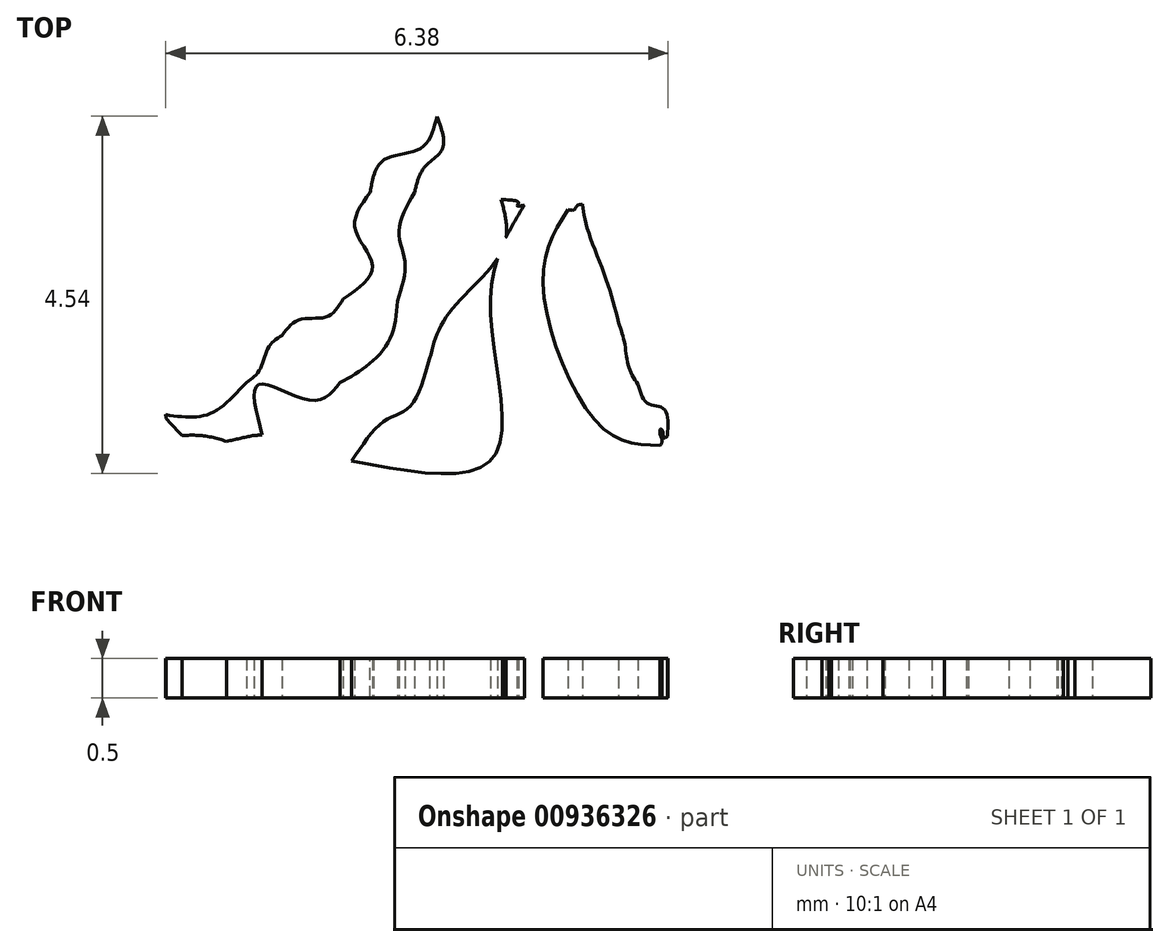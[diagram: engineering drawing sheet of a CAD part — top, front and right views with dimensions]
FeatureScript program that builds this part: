
annotation { "Feature Type Name" : "Feature", "Feature Type Description" : "" }
export const myFeature = defineFeature(function(context is Context, id is Id, definition is map)
    precondition{}
    {
        {
            var Q0;
            Q0=qCreatedBy(makeId("Top.planeOp"),FACE);
            var sketch = newSketch(context, id + "F0", { "sketchPlane" : qUnion([Q0])});
            skFitSpline(sketch, "E0", {"points": [v(-1.48, -0.63) * mm, v(-1.68, -1.04) * mm, v(-2.15, -1.19) * mm, v(-2.32, -1.6) * mm]});
            skFitSpline(sketch, "E1", {"points": [v(-2.32, -1.6) * mm, v(-2.51, -2.06) * mm, v(-2.3, -2.54) * mm, v(-2.66, -2.95) * mm]});
            skFitSpline(sketch, "E2", {"points": [v(-2.66, -2.95) * mm, v(-2.87, -3.18) * mm, v(-3.21, -3.21) * mm, v(-3.44, -3.41) * mm]});
            skFitSpline(sketch, "E3", {"points": [v(-3.44, -3.41) * mm, v(-3.61, -3.57) * mm, v(-3.73, -3.86) * mm, v(-3.9, -4.01) * mm]});
            skFitSpline(sketch, "E4", {"points": [v(-3.9, -4.01) * mm, v(-4.26, -4.36) * mm, v(-4.55, -4.45) * mm, v(-4.92, -4.42) * mm]});
            skFitSpline(sketch, "E5", {"points": [v(-4.92, -4.42) * mm, v(-4.92, -4.44) * mm, v(-4.92, -4.46) * mm, v(-4.91, -4.47) * mm]});
            skFitSpline(sketch, "E6", {"points": [v(-4.91, -4.47) * mm, v(-4.85, -4.55) * mm, v(-4.78, -4.62) * mm, v(-4.71, -4.69) * mm]});
            skFitSpline(sketch, "E7", {"points": [v(-4.71, -4.69) * mm, v(-4.52, -4.69) * mm, v(-4.33, -4.71) * mm, v(-4.15, -4.76) * mm]});
            skFitSpline(sketch, "E8", {"points": [v(-4.15, -4.76) * mm, v(-3.97, -4.72) * mm, v(-3.81, -4.69) * mm, v(-3.7, -4.68) * mm]});
            skFitSpline(sketch, "E9", {"points": [v(-3.7, -4.68) * mm, v(-3.74, -4.04) * mm, v(-3.06, -4.24) * mm, v(-2.7, -4.02) * mm]});
            skFitSpline(sketch, "E10", {"points": [v(-2.7, -4.02) * mm, v(-2.36, -3.8) * mm, v(-2.07, -3.45) * mm, v(-1.98, -2.98) * mm]});
            skFitSpline(sketch, "E11", {"points": [v(-1.98, -2.98) * mm, v(-1.88, -2.48) * mm, v(-1.96, -2.1) * mm, v(-1.76, -1.6) * mm]});
            skFitSpline(sketch, "E12", {"points": [v(-1.76, -1.6) * mm, v(-1.63, -1.28) * mm, v(-1.4, -1.04) * mm, v(-1.48, -0.63) * mm]});
            skFitSpline(sketch, "E13", {"points": [v(3.94, -4.49) * mm, v(3.82, -4.17) * mm, v(3.68, -3.64) * mm, v(3.43, -3.44) * mm]});
            skFitSpline(sketch, "E14", {"points": [v(3.43, -3.44) * mm, v(3.22, -3.27) * mm, v(2.85, -3.43) * mm, v(2.63, -3.2) * mm]});
            skFitSpline(sketch, "E15", {"points": [v(2.63, -3.2) * mm, v(2.34, -2.93) * mm, v(2.34, -2.3) * mm, v(2.2, -1.94) * mm]});
            skFitSpline(sketch, "E16", {"points": [v(2.2, -1.94) * mm, v(1.93, -1.29) * mm, v(1.3, -1.13) * mm, v(1.27, -0.36) * mm]});
            skFitSpline(sketch, "E17", {"points": [v(0.7, -0.56) * mm, v(1.13, -0.9) * mm, v(1.23, -1.34) * mm, v(1.43, -1.84) * mm]});
            skFitSpline(sketch, "E18", {"points": [v(1.43, -1.84) * mm, v(1.58, -2.21) * mm, v(1.64, -2.69) * mm, v(1.8, -3.03) * mm]});
            skFitSpline(sketch, "E19", {"points": [v(1.8, -3.03) * mm, v(2.08, -3.57) * mm, v(2.64, -3.47) * mm, v(3, -3.87) * mm]});
            skFitSpline(sketch, "E20", {"points": [v(3, -3.87) * mm, v(3.29, -4.18) * mm, v(3.34, -4.74) * mm, v(3.94, -4.49) * mm]});
            skFitSpline(sketch, "E21", {"points": [v(-2.15, -1.57) * mm, v(-2.53, -1) * mm, v(-2.79, -0.73) * mm, v(-3.39, -0.68) * mm]});
            skFitSpline(sketch, "E22", {"points": [v(-3.39, -0.68) * mm, v(-3.76, -0.65) * mm, v(-3.98, -0.73) * mm, v(-4.31, -0.48) * mm]});
            skFitSpline(sketch, "E23", {"points": [v(-4.31, -0.48) * mm, v(-4.88, -0.04) * mm, v(-5.85, 0.8) * mm, v(-4.97, 1.37) * mm]});
            skFitSpline(sketch, "E24", {"points": [v(-4.97, 1.37) * mm, v(-4.12, 1.92) * mm, v(-3.04, 1.34) * mm, v(-2.15, 1.29) * mm]});
            skFitSpline(sketch, "E25", {"points": [v(-2.15, 1.29) * mm, v(-1.68, 1.26) * mm, v(-1.22, 1.44) * mm, v(-0.78, 1.43) * mm]});
            skFitSpline(sketch, "E26", {"points": [v(-0.78, 1.43) * mm, v(-0.29, 1.41) * mm, v(0.03, 1.23) * mm, v(0.53, 1.3) * mm]});
            skFitSpline(sketch, "E27", {"points": [v(0.53, 1.3) * mm, v(1.17, 1.37) * mm, v(1.83, 1.4) * mm, v(2.46, 1.22) * mm]});
            skFitSpline(sketch, "E28", {"points": [v(2.46, 1.22) * mm, v(3.17, 1) * mm, v(3.92, 1.01) * mm, v(4.67, 0.94) * mm]});
            skFitSpline(sketch, "E29", {"points": [v(4.67, 0.94) * mm, v(4.73, -0.3) * mm, v(0.98, 0.89) * mm, v(0.38, 0.95) * mm]});
            skFitSpline(sketch, "E30", {"points": [v(-2.46, 0.88) * mm, v(-3.42, 0.83) * mm, v(-4.37, 1.02) * mm, v(-5.33, 1.02) * mm]});
            skFitSpline(sketch, "E31", {"points": [v(0.98, -0.68) * mm, v(1.32, -0.55) * mm, v(1.54, -0.76) * mm, v(1.84, -0.74) * mm]});
            skFitSpline(sketch, "E32", {"points": [v(1.84, -0.74) * mm, v(2.25, -0.71) * mm, v(2.7, -0.42) * mm, v(3.09, -0.27) * mm]});
            skFitSpline(sketch, "E33", {"points": [v(3.09, -0.27) * mm, v(3.47, -0.12) * mm, v(4.31, 0.08) * mm, v(4.44, 0.6) * mm]});
            skFitSpline(sketch, "E34", {"points": [v(2.47, 0.16) * mm, v(2, 0) * mm, v(1.5, -0.5) * mm, v(0.98, -0.68) * mm]});
            skFitSpline(sketch, "E35", {"points": [v(-1.92, -1.23) * mm, v(-1.14, -1.23) * mm, v(-0.57, -1.05) * mm, v(0.17, -0.95) * mm]});
            skFitSpline(sketch, "E36", {"points": [v(0.17, -0.95) * mm, v(0.44, -0.92) * mm, v(1.05, -1.18) * mm, v(1.27, -1.01) * mm]});
            skFitSpline(sketch, "E37", {"points": [v(1.27, -1.01) * mm, v(1.76, -0.64) * mm, v(0.1, -0.55) * mm, v(-0.01, -0.55) * mm]});
            skFitSpline(sketch, "E38", {"points": [v(-3.42, 3.67) * mm, v(-3.16, 3.86) * mm, v(-3.05, 4.17) * mm, v(-2.82, 4.4) * mm]});
            skFitSpline(sketch, "E39", {"points": [v(-2.82, 4.4) * mm, v(-2.53, 4.7) * mm, v(-2.27, 4.78) * mm, v(-1.86, 4.92) * mm]});
            skFitSpline(sketch, "E40", {"points": [v(-1.86, 4.92) * mm, v(-1.22, 5.15) * mm, v(-0.68, 5.33) * mm, v(0.04, 5.24) * mm]});
            skFitSpline(sketch, "E41", {"points": [v(0.04, 5.24) * mm, v(0.42, 5.2) * mm, v(0.38, 5.22) * mm, v(0.65, 5.07) * mm]});
            skFitSpline(sketch, "E42", {"points": [v(0.65, 5.07) * mm, v(0.9, 4.93) * mm, v(0.97, 4.7) * mm, v(1.27, 4.63) * mm]});
            skFitSpline(sketch, "E43", {"points": [v(1.27, 4.63) * mm, v(1.68, 4.54) * mm, v(1.95, 4.72) * mm, v(2.32, 4.41) * mm]});
            skFitSpline(sketch, "E44", {"points": [v(2.32, 4.41) * mm, v(2.64, 4.15) * mm, v(3.12, 3.3) * mm, v(3.07, 2.9) * mm]});
            skFitSpline(sketch, "E45", {"points": [v(3.07, 2.9) * mm, v(2.9, 3.08) * mm, v(2.63, 3.17) * mm, v(2.37, 3.14) * mm]});
            skFitSpline(sketch, "E46", {"points": [v(2.37, 3.14) * mm, v(2.35, 3.7) * mm, v(1.28, 4.03) * mm, v(0.85, 4.22) * mm]});
            skFitSpline(sketch, "E47", {"points": [v(0.85, 4.22) * mm, v(0.22, 4.5) * mm, v(-0.55, 4.69) * mm, v(-1.26, 4.55) * mm]});
            skFitSpline(sketch, "E48", {"points": [v(-1.26, 4.55) * mm, v(-1.86, 4.43) * mm, v(-2.25, 4.18) * mm, v(-2.68, 3.8) * mm]});
            skFitSpline(sketch, "E49", {"points": [v(-2.68, 3.8) * mm, v(-2.96, 3.55) * mm, v(-3.39, 2.9) * mm, v(-3.78, 2.9) * mm]});
            skFitSpline(sketch, "E50", {"points": [v(-3.78, 2.9) * mm, v(-3.93, 3.44) * mm, v(-3.3, 3.45) * mm, v(-3.42, 3.67) * mm]});
            skFitSpline(sketch, "E51", {"points": [v(-0.66, -1.69) * mm, v(-0.64, -2.32) * mm, v(-1.32, -3.14) * mm, v(-1.57, -3.7) * mm]});
            skFitSpline(sketch, "E52", {"points": [v(-1.57, -3.7) * mm, v(-1.83, -4.34) * mm, v(-2.13, -4.5) * mm, v(-2.56, -5.01) * mm]});
            skFitSpline(sketch, "E53", {"points": [v(-2.56, -5.01) * mm, v(-0.75, -4.95) * mm, v(-0.8, -3.01) * mm, v(-0.36, -1.76) * mm]});
            skFitSpline(sketch, "E54", {"points": [v(-0.36, -1.76) * mm, v(-0.45, -1.77) * mm, v(-0.44, -1.73) * mm, v(-0.66, -1.69) * mm]});
            skFitSpline(sketch, "E55", {"points": [v(0.37, -1.75) * mm, v(0.3, -1.77) * mm, v(0.27, -1.82) * mm, v(0.2, -1.82) * mm]});
            skFitSpline(sketch, "E56", {"points": [v(0.2, -1.82) * mm, v(-0.13, -2.74) * mm, v(0.63, -4.59) * mm, v(1.36, -4.81) * mm]});
            skFitSpline(sketch, "E57", {"points": [v(1.36, -4.81) * mm, v(1.39, -4.76) * mm, v(1.36, -4.66) * mm, v(1.36, -4.6) * mm]});
            skFitSpline(sketch, "E58", {"points": [v(1.36, -4.6) * mm, v(1.39, -4.62) * mm, v(1.4, -4.72) * mm, v(1.45, -4.7) * mm]});
            skFitSpline(sketch, "E59", {"points": [v(1.45, -4.7) * mm, v(1.4, -4.35) * mm, v(1.2, -4.28) * mm, v(1.08, -4.04) * mm]});
            skFitSpline(sketch, "E60", {"points": [v(1.08, -4.04) * mm, v(0.96, -3.8) * mm, v(0.91, -3.52) * mm, v(0.83, -3.26) * mm]});
            skFitSpline(sketch, "E61", {"points": [v(0.83, -3.26) * mm, v(0.67, -2.68) * mm, v(0.43, -2.05) * mm, v(0.37, -1.75) * mm]});
            skFitSpline(sketch, "E62.trimOffspring", {"points": [v(0.98, -0.68) * mm, v(1.32, -0.55) * mm, v(1.54, -0.76) * mm, v(1.84, -0.74) * mm]});
            skSolve(sketch);
        }
        {
            var Q0;
            Q0=makeQuery(id+"F0.imprint","IMPRINT",FACE,{"disambiguationData":[TD([[makeQuery(id+"F0.imprint","IMPRINT",EDGE,{"derivedFrom":sQuery(id+"F0.wireOp",EDGE,"E38")}),-1.0]])]});
            var Q1;
            Q1=makeQuery(id+"F0.imprint","IMPRINT",FACE,{"disambiguationData":[TD([[makeQuery(id+"F0.imprint","IMPRINT",EDGE,{"derivedFrom":sQuery(id+"F0.wireOp",EDGE,"E0")}),1.0]])]});
            var Q2;
            Q2=makeQuery(id+"F0.imprint","IMPRINT",FACE,{"disambiguationData":[TD([[makeQuery(id+"F0.imprint","IMPRINT",EDGE,{"derivedFrom":sQuery(id+"F0.wireOp",EDGE,"E51")}),1.0]])]});
            var Q3;
            Q3=makeQuery(id+"F0.imprint","IMPRINT",FACE,{"disambiguationData":[TD([[makeQuery(id+"F0.imprint","IMPRINT",EDGE,{"derivedFrom":sQuery(id+"F0.wireOp",EDGE,"E55")}),1.0]])]});
            extrude(context, id + "F1", {"entities" : qUnion([Q0, Q1, Q2, Q3]), "depth" : 0.5 * mm, "offsetDistance" : 25 * mm});
        }
    });
